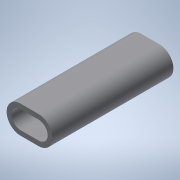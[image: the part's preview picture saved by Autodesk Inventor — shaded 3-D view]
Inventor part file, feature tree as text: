
AUTODESK INVENTOR PART (.ipt)
format: ipt  version: 2020 (Build 240168000, 168)  size: 107,008 bytes
history: native  units: mm
features: extrude x1, sketch x1
ambient origin geometry x8: Origin, YZ Plane, XZ Plane, XY Plane, X Axis, Y Axis, Z Axis, Center Point
bodies: Solid1 (feature_tree)
feature tree (2):
  extrude  "Extrusion1"  Depth=30.0mm
  sketch  "Sketch1"  dims[d0=15.0mm d1=30.0mm d2=8.0mm d3=200.0mm d4=0.0mm]
